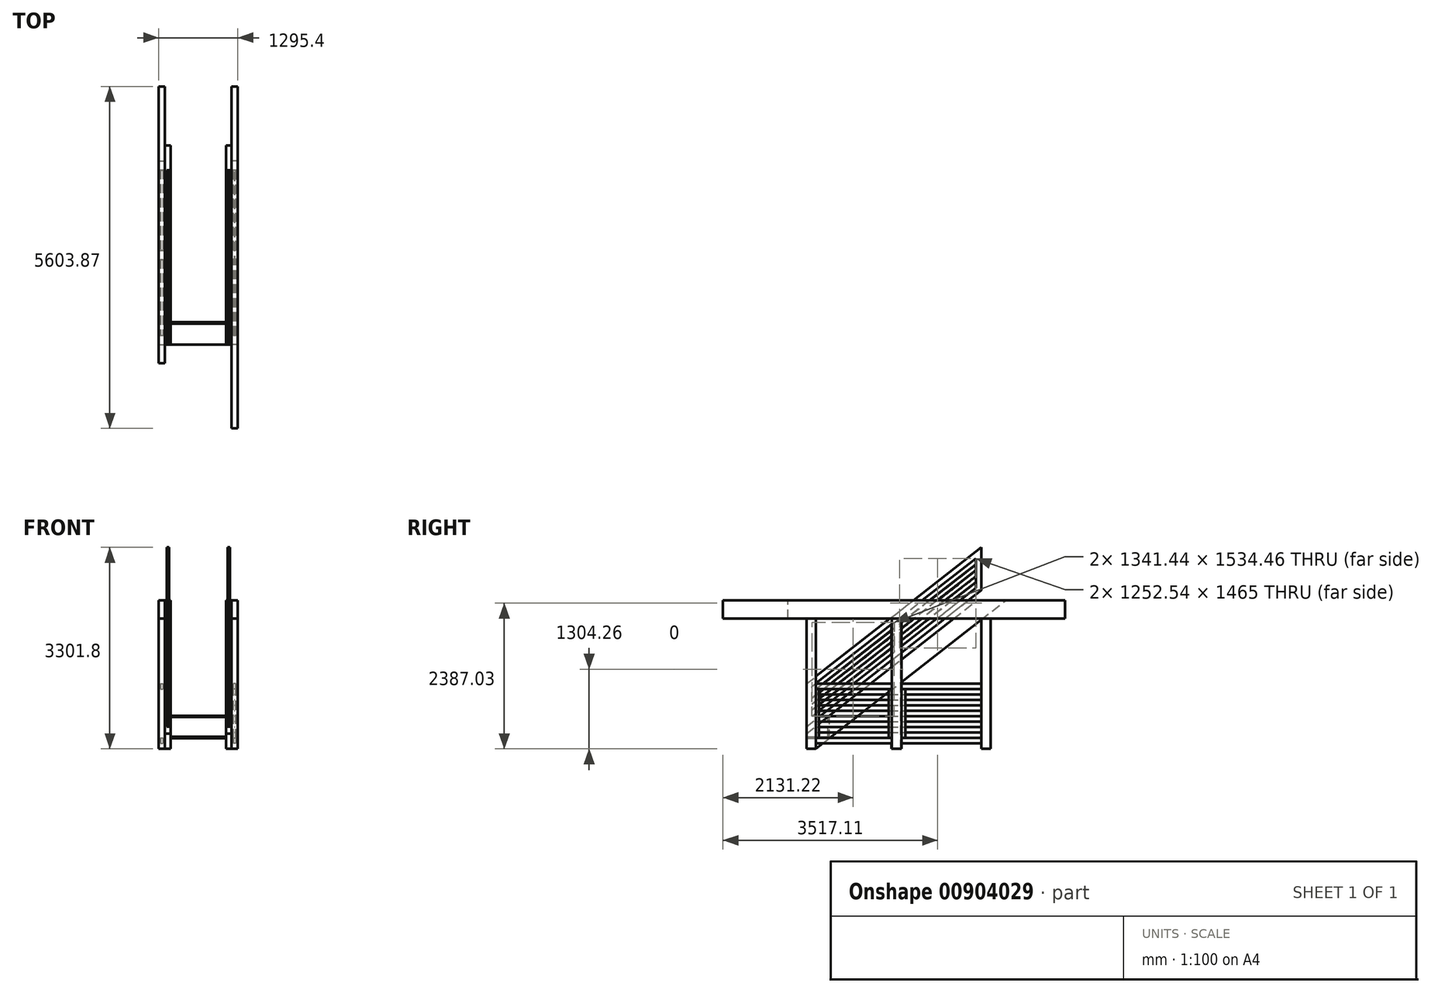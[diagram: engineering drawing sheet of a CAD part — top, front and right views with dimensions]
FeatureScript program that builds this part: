
annotation { "Feature Type Name" : "Feature", "Feature Type Description" : "" }
export const myFeature = defineFeature(function(context is Context, id is Id, definition is map)
    precondition{}
    {
        {
            var Q0;
            Q0=qCreatedBy(makeId("Front.planeOp"),FACE);
            var sketch = newSketch(context, id + "F0", { "sketchPlane" : qUnion([Q0])});
            skLineSegment(sketch, "E0", {"start": v(-546.1, 0) * mm, "end": v(546.1, 0) * mm});
            skSolve(sketch);
        }
        {
            var Q0;
            Q0=sQuery(id+"F0.wireOp",VERTEX,"E0.end");
            var Q1;
            Q1=qCreatedBy(makeId("Right.planeOp"),FACE);
            cPlane(context, id + "F1", {"entities" : qUnion([Q0, Q1]), "cplaneType" : CPlaneType.PLANE_POINT, "offset" : 25.4 * mm, "width" : 152.4 * mm, "height" : 152.4 * mm});
        }
        {
            var Q0;
            Q0=qCreatedBy(id+"F1.planeOp",FACE);
            var sketch = newSketch(context, id + "F2", { "sketchPlane" : qUnion([Q0])});
            skLineSegment(sketch, "E1.bottom", {"start": v(0, 0) * mm, "end": v(152.4, 0) * mm});
            skLineSegment(sketch, "E1.top", {"start": v(0, 2133.6) * mm, "end": v(152.4, 2133.6) * mm});
            skLineSegment(sketch, "E1.left", {"start": v(0, 0) * mm, "end": v(0, 2133.6) * mm});
            skLineSegment(sketch, "E1.right", {"start": v(152.4, 0) * mm, "end": v(152.4, 2133.6) * mm});
            skLineSegment(sketch, "E2.bottom", {"start": v(1397, 0) * mm, "end": v(1552.58, 0) * mm});
            skLineSegment(sketch, "E2.top", {"start": v(1397, 2133.6) * mm, "end": v(1552.57, 2133.6) * mm});
            skLineSegment(sketch, "E2.left", {"start": v(1397, 0) * mm, "end": v(1397, 2133.6) * mm});
            skLineSegment(sketch, "E2.right", {"start": v(1552.58, 0) * mm, "end": v(1552.57, 2133.6) * mm});
            skLineSegment(sketch, "E3.bottom", {"start": v(2860.68, 0) * mm, "end": v(3013.08, 0) * mm});
            skLineSegment(sketch, "E3.top", {"start": v(2860.68, 2133.6) * mm, "end": v(3013.07, 2133.6) * mm});
            skLineSegment(sketch, "E3.left", {"start": v(2860.68, 0) * mm, "end": v(2860.68, 2133.6) * mm});
            skLineSegment(sketch, "E3.right", {"start": v(3013.08, 0) * mm, "end": v(3013.07, 2133.6) * mm});
            skLineSegment(sketch, "E4.bottom", {"start": v(-1371.6, 2432.05) * mm, "end": v(4232.28, 2432.05) * mm});
            skLineSegment(sketch, "E4.top", {"start": v(-1371.6, 2133.6) * mm, "end": v(4232.28, 2133.6) * mm, "construction": true});
            skLineSegment(sketch, "E4.left", {"start": v(-1371.6, 2432.05) * mm, "end": v(-1371.6, 2133.6) * mm});
            skLineSegment(sketch, "E4.right", {"start": v(4232.28, 2432.05) * mm, "end": v(4232.28, 2133.6) * mm});
            skSolve(sketch);
        }
        {
            var Q0;
            Q0=qSketchRegion(id+"F2",true);
            extrude(context, id + "F3", {"entities" : qUnion([Q0]), "depth" : 101.6 * mm, "offsetDistance" : 25.4 * mm});
        }
        {
            var Q0;
            Q0=sQuery(id+"F0.wireOp",VERTEX,"E0.start");
            var Q1;
            Q1=qCreatedBy(makeId("Right.planeOp"),FACE);
            cPlane(context, id + "F4", {"entities" : qUnion([Q0, Q1]), "cplaneType" : CPlaneType.PLANE_POINT, "offset" : 25.4 * mm, "width" : 152.4 * mm, "height" : 152.4 * mm});
        }
        {
            var Q0;
            Q0=qCreatedBy(id+"F4.planeOp",FACE);
            var sketch = newSketch(context, id + "F5", { "sketchPlane" : qUnion([Q0])});
            skLineSegment(sketch, "E5.bottom", {"start": v(1390.65, 0) * mm, "end": v(1543.05, 0) * mm});
            skLineSegment(sketch, "E5.top", {"start": v(1390.65, 2133.6) * mm, "end": v(1543.05, 2133.6) * mm});
            skLineSegment(sketch, "E5.left", {"start": v(1390.65, 0) * mm, "end": v(1390.65, 2133.6) * mm});
            skLineSegment(sketch, "E5.right", {"start": v(1543.05, 0) * mm, "end": v(1543.05, 2133.6) * mm});
            skLineSegment(sketch, "E6.bottom", {"start": v(2863.85, 0) * mm, "end": v(3009.9, 0) * mm});
            skLineSegment(sketch, "E6.top", {"start": v(2863.85, 2133.6) * mm, "end": v(3009.9, 2133.6) * mm});
            skLineSegment(sketch, "E6.left", {"start": v(2863.85, 0) * mm, "end": v(2863.85, 2133.6) * mm});
            skLineSegment(sketch, "E6.right", {"start": v(3009.9, 0) * mm, "end": v(3009.9, 2133.6) * mm});
            skLineSegment(sketch, "E7.0.0", {"start": v(152.4, 2133.6) * mm, "end": v(0, 2133.6) * mm});
            skLineSegment(sketch, "E7.0.1", {"start": v(0, 2133.6) * mm, "end": v(0, 0) * mm});
            skLineSegment(sketch, "E7.0.2", {"start": v(0, 0) * mm, "end": v(152.4, 0) * mm});
            skLineSegment(sketch, "E7.0.3", {"start": v(152.4, 0) * mm, "end": v(152.4, 2133.6) * mm});
            skSolve(sketch);
        }
        {
            var Q0;
            Q0=qSketchRegion(id+"F5",true);
            extrude(context, id + "F6", {"entities" : qUnion([Q0]), "oppositeDirection" : true, "depth" : 101.6 * mm, "offsetDistance" : 25.4 * mm});
        }
        {
            var Q0;
            Q0=qCreatedBy(id+"F1.planeOp",FACE);
            var sketch = newSketch(context, id + "F7", { "sketchPlane" : qUnion([Q0])});
            skLineSegment(sketch, "E8.0", {"start": v(-1371.6, 2133.6) * mm, "end": v(4232.28, 2133.6) * mm});
            skLineSegment(sketch, "E9.0", {"start": v(-1371.6, 2432.05) * mm, "end": v(-1371.6, 2133.6) * mm});
            skLineSegment(sketch, "E10.0", {"start": v(-1371.6, 2432.05) * mm, "end": v(4232.28, 2432.05) * mm});
            skLineSegment(sketch, "E11.0", {"start": v(4232.28, 2432.05) * mm, "end": v(4232.28, 2133.6) * mm});
            skSolve(sketch);
        }
        {
            var Q0;
            Q0=makeQuery(id+"F7.imprint","IMPRINT",FACE,{"disambiguationData":[TD([[makeQuery(id+"F7.imprint","IMPRINT",EDGE,{"derivedFrom":sQuery(id+"F7.wireOp",EDGE,"E8.0")}),1.0]])]});
            var Q1;
            Q1=makeQuery(id+"F3.opExtrude","CAP_FACE",FACE,{"disambiguationData":[OSD([sQuery(id+"F2.wireOp",EDGE,"E1.bottom"),sQuery(id+"F2.wireOp",EDGE,"E1.top"),sQuery(id+"F2.wireOp",EDGE,"E1.left"),sQuery(id+"F2.wireOp",EDGE,"E1.right")])],"isStart":false});
            extrude(context, id + "F8", {"entities" : qUnion([Q0]), "endBound" : BoundingType.UP_TO_SURFACE, "depth" : 25.4 * mm, "endBoundEntityFace" : qUnion([Q1]), "offsetDistance" : 25.4 * mm});
        }
        {
            var Q0;
            Q0=qCreatedBy(id+"F4.planeOp",FACE);
            var sketch = newSketch(context, id + "F9", { "sketchPlane" : qUnion([Q0])});
            skLineSegment(sketch, "E12.0.0", {"start": v(4232.28, 2432.05) * mm, "end": v(4232.28, 2133.6) * mm});
            skLineSegment(sketch, "E12.0.1", {"start": v(4232.28, 2133.6) * mm, "end": v(-304.8, 2133.6) * mm});
            skLineSegment(sketch, "E12.0.3", {"start": v(-304.8, 2432.05) * mm, "end": v(4232.28, 2432.05) * mm});
            skLineSegment(sketch, "E13", {"start": v(-304.8, 2432.05) * mm, "end": v(-304.8, 2133.6) * mm});
            skPoint(sketch, "E12.0.2.end.orphan", {"position": v(-1371.6, 2432.05) * mm});
            skPoint(sketch, "E14.orphan", {"position": v(-1371.6, 2133.6) * mm});
            skSolve(sketch);
        }
        {
            var Q0;
            Q0=qSketchRegion(id+"F9",true);
            var Q1;
            Q1=makeQuery(id+"F6.opExtrude","CAP_FACE",FACE,{"disambiguationData":[OSD([sQuery(id+"F5.wireOp",EDGE,"E7.0.0"),sQuery(id+"F5.wireOp",EDGE,"E7.0.1"),sQuery(id+"F5.wireOp",EDGE,"E7.0.2"),sQuery(id+"F5.wireOp",EDGE,"E7.0.3")])],"isStart":false});
            extrude(context, id + "F10", {"entities" : qUnion([Q0]), "endBound" : BoundingType.UP_TO_SURFACE, "oppositeDirection" : true, "depth" : 25.4 * mm, "endBoundEntityFace" : qUnion([Q1]), "offsetDistance" : 25.4 * mm});
        }
        {
            var Q0;
            Q0=qCreatedBy(id+"F1.planeOp",FACE);
            var sketch = newSketch(context, id + "F11", { "sketchPlane" : qUnion([Q0])});
            skLineSegment(sketch, "E15.0", {"start": v(0, 0) * mm, "end": v(0, 251.61) * mm});
            skLineSegment(sketch, "E16", {"start": v(0, 251.61) * mm, "end": v(2790.83, 2432.05) * mm});
            skLineSegment(sketch, "E17", {"start": v(152.4, 0) * mm, "end": v(3265.28, 2432.05) * mm});
            skPoint(sketch, "E18.orphan", {"position": v(0, 2133.6) * mm});
            skPoint(sketch, "E19.orphan", {"position": v(152.4, 2133.6) * mm});
            skLineSegment(sketch, "E20.0", {"start": v(0, 0) * mm, "end": v(152.4, 0) * mm});
            skLineSegment(sketch, "E21.0", {"start": v(2790.83, 2432.05) * mm, "end": v(3265.28, 2432.05) * mm});
            skPoint(sketch, "E22.orphan", {"position": v(4232.28, 2432.05) * mm});
            skPoint(sketch, "E23.orphan", {"position": v(-1371.6, 2432.05) * mm});
            skPoint(sketch, "E24.0.end.orphan", {"position": v(3013.07, 2133.6) * mm});
            skPoint(sketch, "E24.0.start.orphan", {"position": v(3013.08, 0) * mm});
            skSolve(sketch);
        }
        {
            var Q0;
            Q0=qSketchRegion(id+"F11",true);
            extrude(context, id + "F12", {"entities" : qUnion([Q0]), "oppositeDirection" : true, "depth" : 92.07 * mm, "offsetDistance" : 25.4 * mm});
        }
        {
            var Q0;
            Q0=makeQuery(id+"F12.opExtrude","SWEPT_BODY",BODY,{"disambiguationData":[OSD([sQuery(id+"F11.wireOp",EDGE,"E15.0"),sQuery(id+"F11.wireOp",EDGE,"E16"),sQuery(id+"F11.wireOp",EDGE,"E17"),sQuery(id+"F11.wireOp",EDGE,"E20.0"),sQuery(id+"F11.wireOp",EDGE,"E21.0")])]});
            var Q1;
            Q1=qCreatedBy(makeId("Right.planeOp"),FACE);
            mirror(context, id + "F13", {"entities" : qUnion([Q0]), "mirrorPlane" : qUnion([Q1])});
        }
        {
            var Q0;
            Q0=makeQuery(id+"F3.opExtrude","CAP_FACE",FACE,{"disambiguationData":[OSD([sQuery(id+"F2.wireOp",EDGE,"E1.bottom"),sQuery(id+"F2.wireOp",EDGE,"E1.top"),sQuery(id+"F2.wireOp",EDGE,"E1.left"),sQuery(id+"F2.wireOp",EDGE,"E1.right")])],"isStart":false});
            var Q1;
            Q1=makeQuery(id+"F2.imprint","IMPRINT",FACE,{"disambiguationData":[TD([[makeQuery(id+"F2.imprint","IMPRINT",EDGE,{"derivedFrom":sQuery(id+"F2.wireOp",EDGE,"E1.bottom")}),1.0]])]});
            cPlane(context, id + "F14", {"entities" : qUnion([Q0, Q1]), "cplaneType" : CPlaneType.MID_PLANE, "offset" : 25.4 * mm, "width" : 152.4 * mm, "height" : 152.4 * mm});
        }
        {
            var Q0;
            Q0=qCreatedBy(id+"F14.planeOp",FACE);
            var sketch = newSketch(context, id + "F15", { "sketchPlane" : qUnion([Q0])});
            skLineSegment(sketch, "E25.0", {"start": v(152.4, 977.9) * mm, "end": v(152.4, 1066.8) * mm});
            skLineSegment(sketch, "E26.0", {"start": v(1397, 977.9) * mm, "end": v(1397, 1066.8) * mm});
            skLineSegment(sketch, "E27.bottom", {"start": v(152.4, 1066.8) * mm, "end": v(1397, 1066.8) * mm});
            skLineSegment(sketch, "E27.top", {"start": v(152.4, 977.9) * mm, "end": v(1397, 977.9) * mm});
            skPoint(sketch, "E28.orphan", {"position": v(152.4, 2133.6) * mm});
            skPoint(sketch, "E29.orphan", {"position": v(1397, 2133.6) * mm});
            skPoint(sketch, "E30.orphan", {"position": v(1397, 0) * mm});
            skPoint(sketch, "E31.orphan", {"position": v(152.4, 0) * mm});
            skLineSegment(sketch, "E32.bottom", {"start": v(1552.58, 1066.8) * mm, "end": v(2860.68, 1066.8) * mm});
            skLineSegment(sketch, "E32.top", {"start": v(1552.58, 977.9) * mm, "end": v(2860.68, 977.9) * mm});
            skLineSegment(sketch, "E32.left", {"start": v(1552.58, 1066.8) * mm, "end": v(1552.58, 977.9) * mm});
            skLineSegment(sketch, "E32.right", {"start": v(2860.68, 1066.8) * mm, "end": v(2860.68, 977.9) * mm});
            skLineSegment(sketch, "E33.bottom", {"start": v(152.4, 177.8) * mm, "end": v(1397, 177.8) * mm});
            skLineSegment(sketch, "E33.top", {"start": v(152.4, 88.9) * mm, "end": v(1397, 88.9) * mm});
            skLineSegment(sketch, "E33.left", {"start": v(152.4, 177.8) * mm, "end": v(152.4, 88.9) * mm});
            skLineSegment(sketch, "E33.right", {"start": v(1397, 177.8) * mm, "end": v(1397, 88.9) * mm});
            skLineSegment(sketch, "E34.bottom", {"start": v(1552.58, 177.8) * mm, "end": v(2860.68, 177.8) * mm});
            skLineSegment(sketch, "E34.top", {"start": v(1552.58, 88.9) * mm, "end": v(2860.68, 88.9) * mm});
            skLineSegment(sketch, "E34.left", {"start": v(1552.58, 177.8) * mm, "end": v(1552.58, 88.9) * mm});
            skLineSegment(sketch, "E34.right", {"start": v(2860.68, 177.8) * mm, "end": v(2860.68, 88.9) * mm});
            skSolve(sketch);
        }
        {
            var Q0;
            Q0=qSketchRegion(id+"F15",true);
            extrude(context, id + "F16", {"entities" : qUnion([Q0]), "endBound" : BoundingType.SYMMETRIC, "depth" : 38.1 * mm, "offsetDistance" : 25.4 * mm});
        }
        {
            var Q0;
            Q0=makeQuery(id+"F16.opExtrude","CAP_EDGE",EDGE,{"disambiguationData":[OSD([sQuery(id+"F15.wireOp",EDGE,"E27.top")])],"isStart":false});
            cPoint(context, id + "F17", {"entities" : qUnion([Q0]), "parameter" : 0.5});
        }
        {
            var Q0;
            Q0=qCreatedBy(id+"F17",VERTEX);
            var Q1;
            Q1=qCreatedBy(makeId("Front.planeOp"),FACE);
            cPlane(context, id + "F18", {"entities" : qUnion([Q0, Q1]), "cplaneType" : CPlaneType.PLANE_POINT, "offset" : 25.4 * mm, "width" : 152.4 * mm, "height" : 152.4 * mm});
        }
        {
            var Q0;
            Q0=qCreatedBy(id+"F18.planeOp",FACE);
            var sketch = newSketch(context, id + "F19", { "sketchPlane" : qUnion([Q0])});
            skLineSegment(sketch, "E35", {"start": v(596.9, 977.9) * mm, "end": v(596.9, 889) * mm, "construction": true});
            skLineSegment(sketch, "E36", {"start": v(596.9, 889) * mm, "end": v(596.9, 800.1) * mm, "construction": true});
            skLineSegment(sketch, "E37", {"start": v(596.9, 800.1) * mm, "end": v(596.9, 711.2) * mm, "construction": true});
            skLineSegment(sketch, "E38", {"start": v(596.9, 711.2) * mm, "end": v(596.9, 622.3) * mm, "construction": true});
            skLineSegment(sketch, "E39", {"start": v(596.9, 622.3) * mm, "end": v(596.9, 533.4) * mm, "construction": true});
            skLineSegment(sketch, "E40", {"start": v(596.9, 533.4) * mm, "end": v(596.9, 444.5) * mm, "construction": true});
            skLineSegment(sketch, "E41", {"start": v(596.9, 444.5) * mm, "end": v(596.9, 355.6) * mm, "construction": true});
            skLineSegment(sketch, "E42", {"start": v(596.9, 355.6) * mm, "end": v(596.9, 266.7) * mm, "construction": true});
            skLineSegment(sketch, "E43", {"start": v(596.9, 266.7) * mm, "end": v(596.9, 177.8) * mm, "construction": true});
            skCircle(sketch, "E44", {"center": v(596.9, 889) * mm, "radius": 1.59 * mm});
            skCircle(sketch, "E45", {"center": v(596.9, 800.1) * mm, "radius": 1.59 * mm});
            skCircle(sketch, "E46", {"center": v(596.9, 711.2) * mm, "radius": 1.59 * mm});
            skCircle(sketch, "E47", {"center": v(596.9, 622.3) * mm, "radius": 1.59 * mm});
            skCircle(sketch, "E48", {"center": v(596.9, 533.4) * mm, "radius": 1.59 * mm});
            skCircle(sketch, "E49", {"center": v(596.9, 444.5) * mm, "radius": 1.59 * mm});
            skCircle(sketch, "E50", {"center": v(596.9, 355.6) * mm, "radius": 1.59 * mm});
            skCircle(sketch, "E51", {"center": v(596.9, 266.7) * mm, "radius": 1.59 * mm});
            skSolve(sketch);
        }
        {
            var Q0;
            Q0 = qSketchRegion(id + "F19", true);
            var Q1;
            Q1=makeQuery(id+"F3.opExtrude","SWEPT_FACE",FACE,{"disambiguationData":[OSD([sQuery(id+"F2.wireOp",EDGE,"E3.left")])]});
            extrude(context, id + "F20", {"entities" : qUnion([Q0]), "endBound" : BoundingType.UP_TO_NEXT, "depth" : 25.4 * mm, "offsetDistance" : 25.4 * mm, "hasSecondDirection" : true, "secondDirectionBound" : SecondDirectionBoundingType.UP_TO_SURFACE, "secondDirectionOppositeDirection" : true, "secondDirectionDepth" : 25.4 * mm, "secondDirectionBoundEntityFace" : qUnion([Q1])});
        }
        {
            var Q0;
            Q0=makeQuery(id+"F6.opExtrude","CAP_FACE",FACE,{"disambiguationData":[OSD([sQuery(id+"F5.wireOp",EDGE,"E7.0.0"),sQuery(id+"F5.wireOp",EDGE,"E7.0.1"),sQuery(id+"F5.wireOp",EDGE,"E7.0.2"),sQuery(id+"F5.wireOp",EDGE,"E7.0.3")])],"isStart":false});
            var Q1;
            Q1=makeQuery(id+"F6.opExtrude","CAP_FACE",FACE,{"disambiguationData":[OSD([sQuery(id+"F5.wireOp",EDGE,"E7.0.0"),sQuery(id+"F5.wireOp",EDGE,"E7.0.1"),sQuery(id+"F5.wireOp",EDGE,"E7.0.2"),sQuery(id+"F5.wireOp",EDGE,"E7.0.3")])],"isStart":true});
            cPlane(context, id + "F21", {"entities" : qUnion([Q0, Q1]), "cplaneType" : CPlaneType.MID_PLANE, "offset" : 25.4 * mm, "width" : 152.4 * mm, "height" : 152.4 * mm});
        }
        {
            var Q0;
            Q0=qCreatedBy(id+"F21.planeOp",FACE);
            var sketch = newSketch(context, id + "F22", { "sketchPlane" : qUnion([Q0])});
            skLineSegment(sketch, "E52.bottom", {"start": v(-1397, 1066.8) * mm, "end": v(-152.4, 1066.8) * mm});
            skLineSegment(sketch, "E52.top", {"start": v(-1397, 977.9) * mm, "end": v(-152.4, 977.9) * mm});
            skLineSegment(sketch, "E52.left", {"start": v(-1397, 1066.8) * mm, "end": v(-1397, 977.9) * mm});
            skLineSegment(sketch, "E52.right", {"start": v(-152.4, 1066.8) * mm, "end": v(-152.4, 977.9) * mm});
            skLineSegment(sketch, "E53.bottom", {"start": v(-1397, 177.8) * mm, "end": v(-152.4, 177.8) * mm});
            skLineSegment(sketch, "E53.top", {"start": v(-1397, 88.9) * mm, "end": v(-152.4, 88.9) * mm});
            skLineSegment(sketch, "E53.left", {"start": v(-1397, 177.8) * mm, "end": v(-1397, 88.9) * mm});
            skLineSegment(sketch, "E53.right", {"start": v(-152.4, 177.8) * mm, "end": v(-152.4, 88.9) * mm});
            skLineSegment(sketch, "E54.bottom", {"start": v(-2860.68, 1066.8) * mm, "end": v(-1552.58, 1066.8) * mm});
            skLineSegment(sketch, "E54.top", {"start": v(-2860.68, 977.9) * mm, "end": v(-1552.58, 977.9) * mm});
            skLineSegment(sketch, "E54.left", {"start": v(-2860.68, 1066.8) * mm, "end": v(-2860.68, 977.9) * mm});
            skLineSegment(sketch, "E54.right", {"start": v(-1552.58, 1066.8) * mm, "end": v(-1552.58, 977.9) * mm});
            skLineSegment(sketch, "E55.bottom", {"start": v(-2860.68, 177.8) * mm, "end": v(-1552.58, 177.8) * mm});
            skLineSegment(sketch, "E55.top", {"start": v(-2860.68, 88.9) * mm, "end": v(-1552.58, 88.9) * mm});
            skLineSegment(sketch, "E55.left", {"start": v(-2860.68, 177.8) * mm, "end": v(-2860.68, 88.9) * mm});
            skLineSegment(sketch, "E55.right", {"start": v(-1552.58, 177.8) * mm, "end": v(-1552.58, 88.9) * mm});
            skSolve(sketch);
        }
        {
            var Q0;
            Q0=qSketchRegion(id+"F22",true);
            extrude(context, id + "F23", {"entities" : qUnion([Q0]), "endBound" : BoundingType.SYMMETRIC, "depth" : 38.1 * mm, "offsetDistance" : 25.4 * mm});
        }
        {
            var Q0;
            Q0=makeQuery(id+"F12.opExtrude","CAP_FACE",FACE,{"disambiguationData":[OSD([sQuery(id+"F11.wireOp",EDGE,"E15.0"),sQuery(id+"F11.wireOp",EDGE,"E16"),sQuery(id+"F11.wireOp",EDGE,"E17"),sQuery(id+"F11.wireOp",EDGE,"E20.0"),sQuery(id+"F11.wireOp",EDGE,"E21.0")])],"isStart":false});
            var Q1;
            Q1=makeQuery(id+"F12.opExtrude","CAP_FACE",FACE,{"disambiguationData":[OSD([sQuery(id+"F11.wireOp",EDGE,"E15.0"),sQuery(id+"F11.wireOp",EDGE,"E16"),sQuery(id+"F11.wireOp",EDGE,"E17"),sQuery(id+"F11.wireOp",EDGE,"E20.0"),sQuery(id+"F11.wireOp",EDGE,"E21.0")])],"isStart":true});
            cPlane(context, id + "F24", {"entities" : qUnion([Q0, Q1]), "cplaneType" : CPlaneType.MID_PLANE, "offset" : 25.4 * mm, "width" : 152.4 * mm, "height" : 152.4 * mm});
        }
        {
            var Q0;
            Q0=qCreatedBy(id+"F24.planeOp",FACE);
            var sketch = newSketch(context, id + "F25", { "sketchPlane" : qUnion([Q0])});
            skLineSegment(sketch, "E56.0", {"start": v(0, 364.43) * mm, "end": v(-2860.68, 2599.43) * mm});
            skLineSegment(sketch, "E57.0", {"start": v(0, 1066.8) * mm, "end": v(-2860.68, 3301.8) * mm});
            skLineSegment(sketch, "E58.0", {"start": v(0, 364.43) * mm, "end": v(0, 1066.8) * mm});
            skPoint(sketch, "E59.orphan", {"position": v(0, 2133.6) * mm});
            skPoint(sketch, "E60.orphan", {"position": v(0, 0) * mm});
            skLineSegment(sketch, "E61", {"start": v(-2860.68, 3301.8) * mm, "end": v(-2860.68, 2599.43) * mm});
            skLineSegment(sketch, "E62.0", {"start": v(-88.9, 1023.44) * mm, "end": v(-2771.78, 3119.53) * mm});
            skLineSegment(sketch, "E63.0", {"start": v(-88.9, 537.03) * mm, "end": v(-88.9, 1023.44) * mm});
            skLineSegment(sketch, "E64.trimOffspring", {"start": v(-2771.78, 3119.53) * mm, "end": v(-2771.78, 2633.12) * mm});
            skLineSegment(sketch, "E65.trimOffspring", {"start": v(-88.9, 537.03) * mm, "end": v(-2771.78, 2633.12) * mm});
            skLineSegment(sketch, "E66", {"start": v(-88.9, 1023.44) * mm, "end": v(0, 1066.8) * mm});
            skLineSegment(sketch, "E67", {"start": v(0, 364.43) * mm, "end": v(-88.9, 537.03) * mm});
            skLineSegment(sketch, "E68", {"start": v(-2771.78, 3119.53) * mm, "end": v(-2860.68, 3301.8) * mm});
            skLineSegment(sketch, "E69", {"start": v(-2771.78, 2633.12) * mm, "end": v(-2860.68, 2599.43) * mm});
            skPoint(sketch, "E70.0.start.orphan", {"position": v(-1552.58, 0) * mm});
            skPoint(sketch, "E71.0.start.orphan", {"position": v(-1397, 0) * mm});
            skLineSegment(sketch, "E72", {"start": v(-1397, 2045.44) * mm, "end": v(-1552.57, 2045.44) * mm, "construction": true});
            skLineSegment(sketch, "E73", {"start": v(-1474.79, 2045.44) * mm, "end": v(-1474.79, 1619.8) * mm, "construction": true});
            skLineSegment(sketch, "E74", {"start": v(-1430.34, 2071.49) * mm, "end": v(-1430.34, 1585.08) * mm});
            skLineSegment(sketch, "E75.MirrorCS", {"start": v(-1519.24, 2140.94) * mm, "end": v(-1519.24, 1654.53) * mm});
            skLineSegment(sketch, "E76", {"start": v(-1474.79, 1619.8) * mm, "end": v(-1238.8, 1921.85) * mm, "construction": true});
            skSolve(sketch);
        }
        {
            var Q0;
            Q0=makeQuery(id+"F25.imprint","IMPRINT",FACE,{"disambiguationData":[TD([[makeQuery(id+"F25.imprint","IMPRINT",EDGE,{"derivedFrom":sQuery(id+"F25.wireOp",EDGE,"E57.0")}),1.0]])]});
            var Q1;
            Q1=makeQuery(id+"F25.imprint","IMPRINT",FACE,{"disambiguationData":[TD([[makeQuery(id+"F25.imprint","IMPRINT",EDGE,{"derivedFrom":sQuery(id+"F25.wireOp",EDGE,"E61")}),1.0]])]});
            var Q2;
            Q2=makeQuery(id+"F25.imprint","IMPRINT",FACE,{"disambiguationData":[TD([[makeQuery(id+"F25.imprint","IMPRINT",EDGE,{"derivedFrom":sQuery(id+"F25.wireOp",EDGE,"E56.0")}),-1.0]])]});
            var Q3;
            Q3=makeQuery(id+"F25.imprint","IMPRINT",FACE,{"disambiguationData":[TD([[makeQuery(id+"F25.imprint","IMPRINT",EDGE,{"derivedFrom":sQuery(id+"F25.wireOp",EDGE,"E58.0")}),1.0]])]});
            var Q4;
            {var subQ0=sQuery(id+"F25.wireOp",EDGE,"E74");Q4=makeQuery(id+"F25.imprint","IMPRINT",FACE,{"disambiguationData":[TD([[makeQuery(id+"F25.imprint","IMPRINT",EDGE,{"derivedFrom":subQ0}),-1.0]])]});}
            extrude(context, id + "F26", {"entities" : qUnion([Q0, Q1, Q2, Q3, Q4]), "endBound" : BoundingType.SYMMETRIC, "depth" : 38.1 * mm, "offsetDistance" : 25.4 * mm});
        }
        {
            var Q0;
            Q0=makeQuery(id+"FHlwvRDlp0Xm9cG_28.opPattern","COPY",BODY,{"derivedFrom":makeQuery(id+"F8SUDAKNwE7EsUo_26.opExtrude","SWEPT_BODY",BODY,{"disambiguationData":[OSD([sQuery(id+"FL15oFyUtI3aBrd_26.wireOp",EDGE,"VrMjjD4X-CYQ3-yA4v-7hPQ-fvzbZlASwizG"),sQuery(id+"FL15oFyUtI3aBrd_26.wireOp",EDGE,"w2hLujtV-I2TP-pglX-lp1i-IlIAiG8QoFdS"),sQuery(id+"FL15oFyUtI3aBrd_26.wireOp",EDGE,"Haosjz9O-undc-fuWQ-oRTa-weX78iZNw2A3"),sQuery(id+"FL15oFyUtI3aBrd_26.wireOp",EDGE,"bgq73AYN-j48V-VU7J-jVlr-Mn434VgHHMK9")])]}),"instanceName":"6"});
            var Q1;
            Q1=makeQuery(id+"FHlwvRDlp0Xm9cG_28.opPattern","COPY",BODY,{"derivedFrom":makeQuery(id+"F8SUDAKNwE7EsUo_26.opExtrude","SWEPT_BODY",BODY,{"disambiguationData":[OSD([sQuery(id+"FL15oFyUtI3aBrd_26.wireOp",EDGE,"VrMjjD4X-CYQ3-yA4v-7hPQ-fvzbZlASwizG"),sQuery(id+"FL15oFyUtI3aBrd_26.wireOp",EDGE,"w2hLujtV-I2TP-pglX-lp1i-IlIAiG8QoFdS"),sQuery(id+"FL15oFyUtI3aBrd_26.wireOp",EDGE,"Haosjz9O-undc-fuWQ-oRTa-weX78iZNw2A3"),sQuery(id+"FL15oFyUtI3aBrd_26.wireOp",EDGE,"bgq73AYN-j48V-VU7J-jVlr-Mn434VgHHMK9")])]}),"instanceName":"5"});
            var Q2;
            Q2=makeQuery(id+"FHlwvRDlp0Xm9cG_28.opPattern","COPY",BODY,{"derivedFrom":makeQuery(id+"F8SUDAKNwE7EsUo_26.opExtrude","SWEPT_BODY",BODY,{"disambiguationData":[OSD([sQuery(id+"FL15oFyUtI3aBrd_26.wireOp",EDGE,"VrMjjD4X-CYQ3-yA4v-7hPQ-fvzbZlASwizG"),sQuery(id+"FL15oFyUtI3aBrd_26.wireOp",EDGE,"w2hLujtV-I2TP-pglX-lp1i-IlIAiG8QoFdS"),sQuery(id+"FL15oFyUtI3aBrd_26.wireOp",EDGE,"Haosjz9O-undc-fuWQ-oRTa-weX78iZNw2A3"),sQuery(id+"FL15oFyUtI3aBrd_26.wireOp",EDGE,"bgq73AYN-j48V-VU7J-jVlr-Mn434VgHHMK9")])]}),"instanceName":"4"});
            var Q3;
            Q3=makeQuery(id+"F2WfsVXshQW02Ji_28.opPattern","COPY",BODY,{"derivedFrom":makeQuery(id+"F8SUDAKNwE7EsUo_26.opExtrude","SWEPT_BODY",BODY,{"disambiguationData":[OSD([sQuery(id+"FL15oFyUtI3aBrd_26.wireOp",EDGE,"VrMjjD4X-CYQ3-yA4v-7hPQ-fvzbZlASwizG"),sQuery(id+"FL15oFyUtI3aBrd_26.wireOp",EDGE,"w2hLujtV-I2TP-pglX-lp1i-IlIAiG8QoFdS"),sQuery(id+"FL15oFyUtI3aBrd_26.wireOp",EDGE,"Haosjz9O-undc-fuWQ-oRTa-weX78iZNw2A3"),sQuery(id+"FL15oFyUtI3aBrd_26.wireOp",EDGE,"bgq73AYN-j48V-VU7J-jVlr-Mn434VgHHMK9")])]}),"instanceName":"1"});
            var Q4;
            Q4=makeQuery(id+"F2WfsVXshQW02Ji_28.opPattern","COPY",BODY,{"derivedFrom":makeQuery(id+"F8SUDAKNwE7EsUo_26.opExtrude","SWEPT_BODY",BODY,{"disambiguationData":[OSD([sQuery(id+"FL15oFyUtI3aBrd_26.wireOp",EDGE,"VrMjjD4X-CYQ3-yA4v-7hPQ-fvzbZlASwizG"),sQuery(id+"FL15oFyUtI3aBrd_26.wireOp",EDGE,"w2hLujtV-I2TP-pglX-lp1i-IlIAiG8QoFdS"),sQuery(id+"FL15oFyUtI3aBrd_26.wireOp",EDGE,"Haosjz9O-undc-fuWQ-oRTa-weX78iZNw2A3"),sQuery(id+"FL15oFyUtI3aBrd_26.wireOp",EDGE,"bgq73AYN-j48V-VU7J-jVlr-Mn434VgHHMK9")])]}),"instanceName":"2"});
            var Q5;
            Q5=makeQuery(id+"F2WfsVXshQW02Ji_28.opPattern","COPY",BODY,{"derivedFrom":makeQuery(id+"F8SUDAKNwE7EsUo_26.opExtrude","SWEPT_BODY",BODY,{"disambiguationData":[OSD([sQuery(id+"FL15oFyUtI3aBrd_26.wireOp",EDGE,"VrMjjD4X-CYQ3-yA4v-7hPQ-fvzbZlASwizG"),sQuery(id+"FL15oFyUtI3aBrd_26.wireOp",EDGE,"w2hLujtV-I2TP-pglX-lp1i-IlIAiG8QoFdS"),sQuery(id+"FL15oFyUtI3aBrd_26.wireOp",EDGE,"Haosjz9O-undc-fuWQ-oRTa-weX78iZNw2A3"),sQuery(id+"FL15oFyUtI3aBrd_26.wireOp",EDGE,"bgq73AYN-j48V-VU7J-jVlr-Mn434VgHHMK9")])]}),"instanceName":"3"});
            var Q6;
            Q6=makeQuery(id+"F2WfsVXshQW02Ji_28.opPattern","COPY",BODY,{"derivedFrom":makeQuery(id+"F8SUDAKNwE7EsUo_26.opExtrude","SWEPT_BODY",BODY,{"disambiguationData":[OSD([sQuery(id+"FL15oFyUtI3aBrd_26.wireOp",EDGE,"VrMjjD4X-CYQ3-yA4v-7hPQ-fvzbZlASwizG"),sQuery(id+"FL15oFyUtI3aBrd_26.wireOp",EDGE,"w2hLujtV-I2TP-pglX-lp1i-IlIAiG8QoFdS"),sQuery(id+"FL15oFyUtI3aBrd_26.wireOp",EDGE,"Haosjz9O-undc-fuWQ-oRTa-weX78iZNw2A3"),sQuery(id+"FL15oFyUtI3aBrd_26.wireOp",EDGE,"bgq73AYN-j48V-VU7J-jVlr-Mn434VgHHMK9")])]}),"instanceName":"4"});
            var Q7;
            Q7=makeQuery(id+"F2WfsVXshQW02Ji_28.opPattern","COPY",BODY,{"derivedFrom":makeQuery(id+"F8SUDAKNwE7EsUo_26.opExtrude","SWEPT_BODY",BODY,{"disambiguationData":[OSD([sQuery(id+"FL15oFyUtI3aBrd_26.wireOp",EDGE,"VrMjjD4X-CYQ3-yA4v-7hPQ-fvzbZlASwizG"),sQuery(id+"FL15oFyUtI3aBrd_26.wireOp",EDGE,"w2hLujtV-I2TP-pglX-lp1i-IlIAiG8QoFdS"),sQuery(id+"FL15oFyUtI3aBrd_26.wireOp",EDGE,"Haosjz9O-undc-fuWQ-oRTa-weX78iZNw2A3"),sQuery(id+"FL15oFyUtI3aBrd_26.wireOp",EDGE,"bgq73AYN-j48V-VU7J-jVlr-Mn434VgHHMK9")])]}),"instanceName":"5"});
            var Q8;
            Q8=makeQuery(id+"F2WfsVXshQW02Ji_28.opPattern","COPY",BODY,{"derivedFrom":makeQuery(id+"F8SUDAKNwE7EsUo_26.opExtrude","SWEPT_BODY",BODY,{"disambiguationData":[OSD([sQuery(id+"FL15oFyUtI3aBrd_26.wireOp",EDGE,"VrMjjD4X-CYQ3-yA4v-7hPQ-fvzbZlASwizG"),sQuery(id+"FL15oFyUtI3aBrd_26.wireOp",EDGE,"w2hLujtV-I2TP-pglX-lp1i-IlIAiG8QoFdS"),sQuery(id+"FL15oFyUtI3aBrd_26.wireOp",EDGE,"Haosjz9O-undc-fuWQ-oRTa-weX78iZNw2A3"),sQuery(id+"FL15oFyUtI3aBrd_26.wireOp",EDGE,"bgq73AYN-j48V-VU7J-jVlr-Mn434VgHHMK9")])]}),"instanceName":"6"});
            var Q9;
            Q9=makeQuery(id+"FHlwvRDlp0Xm9cG_28.opPattern","COPY",BODY,{"derivedFrom":makeQuery(id+"F8SUDAKNwE7EsUo_26.opExtrude","SWEPT_BODY",BODY,{"disambiguationData":[OSD([sQuery(id+"FL15oFyUtI3aBrd_26.wireOp",EDGE,"VrMjjD4X-CYQ3-yA4v-7hPQ-fvzbZlASwizG"),sQuery(id+"FL15oFyUtI3aBrd_26.wireOp",EDGE,"w2hLujtV-I2TP-pglX-lp1i-IlIAiG8QoFdS"),sQuery(id+"FL15oFyUtI3aBrd_26.wireOp",EDGE,"Haosjz9O-undc-fuWQ-oRTa-weX78iZNw2A3"),sQuery(id+"FL15oFyUtI3aBrd_26.wireOp",EDGE,"bgq73AYN-j48V-VU7J-jVlr-Mn434VgHHMK9")])]}),"instanceName":"1"});
            var Q10;
            Q10=makeQuery(id+"FHlwvRDlp0Xm9cG_28.opPattern","COPY",BODY,{"derivedFrom":makeQuery(id+"F8SUDAKNwE7EsUo_26.opExtrude","SWEPT_BODY",BODY,{"disambiguationData":[OSD([sQuery(id+"FL15oFyUtI3aBrd_26.wireOp",EDGE,"VrMjjD4X-CYQ3-yA4v-7hPQ-fvzbZlASwizG"),sQuery(id+"FL15oFyUtI3aBrd_26.wireOp",EDGE,"w2hLujtV-I2TP-pglX-lp1i-IlIAiG8QoFdS"),sQuery(id+"FL15oFyUtI3aBrd_26.wireOp",EDGE,"Haosjz9O-undc-fuWQ-oRTa-weX78iZNw2A3"),sQuery(id+"FL15oFyUtI3aBrd_26.wireOp",EDGE,"bgq73AYN-j48V-VU7J-jVlr-Mn434VgHHMK9")])]}),"instanceName":"2"});
            var Q11;
            Q11=makeQuery(id+"FHlwvRDlp0Xm9cG_28.opPattern","COPY",BODY,{"derivedFrom":makeQuery(id+"F8SUDAKNwE7EsUo_26.opExtrude","SWEPT_BODY",BODY,{"disambiguationData":[OSD([sQuery(id+"FL15oFyUtI3aBrd_26.wireOp",EDGE,"VrMjjD4X-CYQ3-yA4v-7hPQ-fvzbZlASwizG"),sQuery(id+"FL15oFyUtI3aBrd_26.wireOp",EDGE,"w2hLujtV-I2TP-pglX-lp1i-IlIAiG8QoFdS"),sQuery(id+"FL15oFyUtI3aBrd_26.wireOp",EDGE,"Haosjz9O-undc-fuWQ-oRTa-weX78iZNw2A3"),sQuery(id+"FL15oFyUtI3aBrd_26.wireOp",EDGE,"bgq73AYN-j48V-VU7J-jVlr-Mn434VgHHMK9")])]}),"instanceName":"3"});
            var Q12;
            Q12=makeQuery(id+"FeZcZVifgtCtkFP_28.opPattern","COPY",BODY,{"derivedFrom":makeQuery(id+"F8SUDAKNwE7EsUo_26.opExtrude","SWEPT_BODY",BODY,{"disambiguationData":[OSD([sQuery(id+"FL15oFyUtI3aBrd_26.wireOp",EDGE,"r1ENYqX6-6cbb-IXZZ-OYHh-hil2T0saHPIk"),sQuery(id+"FL15oFyUtI3aBrd_26.wireOp",EDGE,"urqhdUsR-mYzn-lPOw-VYYU-hiYjFugUIPjQ"),sQuery(id+"FL15oFyUtI3aBrd_26.wireOp",EDGE,"n4ZBWz9C-kEvr-YDfq-9QLi-Q9yPjt8Ly8hL"),sQuery(id+"FL15oFyUtI3aBrd_26.wireOp",EDGE,"e2zvSQfy-2Bil-96lf-zHMV-ZBLVYw9i9ZqR")])]}),"instanceName":"4"});
            var Q13;
            Q13=makeQuery(id+"FeZcZVifgtCtkFP_28.opPattern","COPY",BODY,{"derivedFrom":makeQuery(id+"F8SUDAKNwE7EsUo_26.opExtrude","SWEPT_BODY",BODY,{"disambiguationData":[OSD([sQuery(id+"FL15oFyUtI3aBrd_26.wireOp",EDGE,"r1ENYqX6-6cbb-IXZZ-OYHh-hil2T0saHPIk"),sQuery(id+"FL15oFyUtI3aBrd_26.wireOp",EDGE,"urqhdUsR-mYzn-lPOw-VYYU-hiYjFugUIPjQ"),sQuery(id+"FL15oFyUtI3aBrd_26.wireOp",EDGE,"n4ZBWz9C-kEvr-YDfq-9QLi-Q9yPjt8Ly8hL"),sQuery(id+"FL15oFyUtI3aBrd_26.wireOp",EDGE,"e2zvSQfy-2Bil-96lf-zHMV-ZBLVYw9i9ZqR")])]}),"instanceName":"5"});
            var Q14;
            Q14=makeQuery(id+"FeZcZVifgtCtkFP_28.opPattern","COPY",BODY,{"derivedFrom":makeQuery(id+"F8SUDAKNwE7EsUo_26.opExtrude","SWEPT_BODY",BODY,{"disambiguationData":[OSD([sQuery(id+"FL15oFyUtI3aBrd_26.wireOp",EDGE,"r1ENYqX6-6cbb-IXZZ-OYHh-hil2T0saHPIk"),sQuery(id+"FL15oFyUtI3aBrd_26.wireOp",EDGE,"urqhdUsR-mYzn-lPOw-VYYU-hiYjFugUIPjQ"),sQuery(id+"FL15oFyUtI3aBrd_26.wireOp",EDGE,"n4ZBWz9C-kEvr-YDfq-9QLi-Q9yPjt8Ly8hL"),sQuery(id+"FL15oFyUtI3aBrd_26.wireOp",EDGE,"e2zvSQfy-2Bil-96lf-zHMV-ZBLVYw9i9ZqR")])]}),"instanceName":"6"});
            var Q15;
            Q15=makeQuery(id+"FeZcZVifgtCtkFP_28.opPattern","COPY",BODY,{"derivedFrom":makeQuery(id+"F8SUDAKNwE7EsUo_26.opExtrude","SWEPT_BODY",BODY,{"disambiguationData":[OSD([sQuery(id+"FL15oFyUtI3aBrd_26.wireOp",EDGE,"r1ENYqX6-6cbb-IXZZ-OYHh-hil2T0saHPIk"),sQuery(id+"FL15oFyUtI3aBrd_26.wireOp",EDGE,"urqhdUsR-mYzn-lPOw-VYYU-hiYjFugUIPjQ"),sQuery(id+"FL15oFyUtI3aBrd_26.wireOp",EDGE,"n4ZBWz9C-kEvr-YDfq-9QLi-Q9yPjt8Ly8hL"),sQuery(id+"FL15oFyUtI3aBrd_26.wireOp",EDGE,"e2zvSQfy-2Bil-96lf-zHMV-ZBLVYw9i9ZqR")])]}),"instanceName":"7"});
            var Q16;
            Q16=makeQuery(id+"FVkHQME55aZ6rBw_28.opPattern","COPY",BODY,{"derivedFrom":makeQuery(id+"F8SUDAKNwE7EsUo_26.opExtrude","SWEPT_BODY",BODY,{"disambiguationData":[OSD([sQuery(id+"FL15oFyUtI3aBrd_26.wireOp",EDGE,"r1ENYqX6-6cbb-IXZZ-OYHh-hil2T0saHPIk"),sQuery(id+"FL15oFyUtI3aBrd_26.wireOp",EDGE,"urqhdUsR-mYzn-lPOw-VYYU-hiYjFugUIPjQ"),sQuery(id+"FL15oFyUtI3aBrd_26.wireOp",EDGE,"n4ZBWz9C-kEvr-YDfq-9QLi-Q9yPjt8Ly8hL"),sQuery(id+"FL15oFyUtI3aBrd_26.wireOp",EDGE,"e2zvSQfy-2Bil-96lf-zHMV-ZBLVYw9i9ZqR")])]}),"instanceName":"1"});
            var Q17;
            Q17=makeQuery(id+"FVkHQME55aZ6rBw_28.opPattern","COPY",BODY,{"derivedFrom":makeQuery(id+"F8SUDAKNwE7EsUo_26.opExtrude","SWEPT_BODY",BODY,{"disambiguationData":[OSD([sQuery(id+"FL15oFyUtI3aBrd_26.wireOp",EDGE,"r1ENYqX6-6cbb-IXZZ-OYHh-hil2T0saHPIk"),sQuery(id+"FL15oFyUtI3aBrd_26.wireOp",EDGE,"urqhdUsR-mYzn-lPOw-VYYU-hiYjFugUIPjQ"),sQuery(id+"FL15oFyUtI3aBrd_26.wireOp",EDGE,"n4ZBWz9C-kEvr-YDfq-9QLi-Q9yPjt8Ly8hL"),sQuery(id+"FL15oFyUtI3aBrd_26.wireOp",EDGE,"e2zvSQfy-2Bil-96lf-zHMV-ZBLVYw9i9ZqR")])]}),"instanceName":"2"});
            var Q18;
            Q18=makeQuery(id+"FVkHQME55aZ6rBw_28.opPattern","COPY",BODY,{"derivedFrom":makeQuery(id+"F8SUDAKNwE7EsUo_26.opExtrude","SWEPT_BODY",BODY,{"disambiguationData":[OSD([sQuery(id+"FL15oFyUtI3aBrd_26.wireOp",EDGE,"r1ENYqX6-6cbb-IXZZ-OYHh-hil2T0saHPIk"),sQuery(id+"FL15oFyUtI3aBrd_26.wireOp",EDGE,"urqhdUsR-mYzn-lPOw-VYYU-hiYjFugUIPjQ"),sQuery(id+"FL15oFyUtI3aBrd_26.wireOp",EDGE,"n4ZBWz9C-kEvr-YDfq-9QLi-Q9yPjt8Ly8hL"),sQuery(id+"FL15oFyUtI3aBrd_26.wireOp",EDGE,"e2zvSQfy-2Bil-96lf-zHMV-ZBLVYw9i9ZqR")])]}),"instanceName":"3"});
            var Q19;
            Q19=makeQuery(id+"FVkHQME55aZ6rBw_28.opPattern","COPY",BODY,{"derivedFrom":makeQuery(id+"F8SUDAKNwE7EsUo_26.opExtrude","SWEPT_BODY",BODY,{"disambiguationData":[OSD([sQuery(id+"FL15oFyUtI3aBrd_26.wireOp",EDGE,"r1ENYqX6-6cbb-IXZZ-OYHh-hil2T0saHPIk"),sQuery(id+"FL15oFyUtI3aBrd_26.wireOp",EDGE,"urqhdUsR-mYzn-lPOw-VYYU-hiYjFugUIPjQ"),sQuery(id+"FL15oFyUtI3aBrd_26.wireOp",EDGE,"n4ZBWz9C-kEvr-YDfq-9QLi-Q9yPjt8Ly8hL"),sQuery(id+"FL15oFyUtI3aBrd_26.wireOp",EDGE,"e2zvSQfy-2Bil-96lf-zHMV-ZBLVYw9i9ZqR")])]}),"instanceName":"4"});
            var Q20;
            Q20=makeQuery(id+"FVkHQME55aZ6rBw_28.opPattern","COPY",BODY,{"derivedFrom":makeQuery(id+"F8SUDAKNwE7EsUo_26.opExtrude","SWEPT_BODY",BODY,{"disambiguationData":[OSD([sQuery(id+"FL15oFyUtI3aBrd_26.wireOp",EDGE,"r1ENYqX6-6cbb-IXZZ-OYHh-hil2T0saHPIk"),sQuery(id+"FL15oFyUtI3aBrd_26.wireOp",EDGE,"urqhdUsR-mYzn-lPOw-VYYU-hiYjFugUIPjQ"),sQuery(id+"FL15oFyUtI3aBrd_26.wireOp",EDGE,"n4ZBWz9C-kEvr-YDfq-9QLi-Q9yPjt8Ly8hL"),sQuery(id+"FL15oFyUtI3aBrd_26.wireOp",EDGE,"e2zvSQfy-2Bil-96lf-zHMV-ZBLVYw9i9ZqR")])]}),"instanceName":"5"});
            var Q21;
            Q21=makeQuery(id+"FVkHQME55aZ6rBw_28.opPattern","COPY",BODY,{"derivedFrom":makeQuery(id+"F8SUDAKNwE7EsUo_26.opExtrude","SWEPT_BODY",BODY,{"disambiguationData":[OSD([sQuery(id+"FL15oFyUtI3aBrd_26.wireOp",EDGE,"r1ENYqX6-6cbb-IXZZ-OYHh-hil2T0saHPIk"),sQuery(id+"FL15oFyUtI3aBrd_26.wireOp",EDGE,"urqhdUsR-mYzn-lPOw-VYYU-hiYjFugUIPjQ"),sQuery(id+"FL15oFyUtI3aBrd_26.wireOp",EDGE,"n4ZBWz9C-kEvr-YDfq-9QLi-Q9yPjt8Ly8hL"),sQuery(id+"FL15oFyUtI3aBrd_26.wireOp",EDGE,"e2zvSQfy-2Bil-96lf-zHMV-ZBLVYw9i9ZqR")])]}),"instanceName":"6"});
            var Q22;
            Q22=makeQuery(id+"FVkHQME55aZ6rBw_28.opPattern","COPY",BODY,{"derivedFrom":makeQuery(id+"F8SUDAKNwE7EsUo_26.opExtrude","SWEPT_BODY",BODY,{"disambiguationData":[OSD([sQuery(id+"FL15oFyUtI3aBrd_26.wireOp",EDGE,"r1ENYqX6-6cbb-IXZZ-OYHh-hil2T0saHPIk"),sQuery(id+"FL15oFyUtI3aBrd_26.wireOp",EDGE,"urqhdUsR-mYzn-lPOw-VYYU-hiYjFugUIPjQ"),sQuery(id+"FL15oFyUtI3aBrd_26.wireOp",EDGE,"n4ZBWz9C-kEvr-YDfq-9QLi-Q9yPjt8Ly8hL"),sQuery(id+"FL15oFyUtI3aBrd_26.wireOp",EDGE,"e2zvSQfy-2Bil-96lf-zHMV-ZBLVYw9i9ZqR")])]}),"instanceName":"7"});
            var Q23;
            Q23=makeQuery(id+"F8SUDAKNwE7EsUo_26.opExtrude","SWEPT_BODY",BODY,{"disambiguationData":[OSD([sQuery(id+"FL15oFyUtI3aBrd_26.wireOp",EDGE,"VrMjjD4X-CYQ3-yA4v-7hPQ-fvzbZlASwizG"),sQuery(id+"FL15oFyUtI3aBrd_26.wireOp",EDGE,"w2hLujtV-I2TP-pglX-lp1i-IlIAiG8QoFdS"),sQuery(id+"FL15oFyUtI3aBrd_26.wireOp",EDGE,"Haosjz9O-undc-fuWQ-oRTa-weX78iZNw2A3"),sQuery(id+"FL15oFyUtI3aBrd_26.wireOp",EDGE,"bgq73AYN-j48V-VU7J-jVlr-Mn434VgHHMK9")])]});
            var Q24;
            Q24=makeQuery(id+"FeZcZVifgtCtkFP_28.opPattern","COPY",BODY,{"derivedFrom":makeQuery(id+"F8SUDAKNwE7EsUo_26.opExtrude","SWEPT_BODY",BODY,{"disambiguationData":[OSD([sQuery(id+"FL15oFyUtI3aBrd_26.wireOp",EDGE,"r1ENYqX6-6cbb-IXZZ-OYHh-hil2T0saHPIk"),sQuery(id+"FL15oFyUtI3aBrd_26.wireOp",EDGE,"urqhdUsR-mYzn-lPOw-VYYU-hiYjFugUIPjQ"),sQuery(id+"FL15oFyUtI3aBrd_26.wireOp",EDGE,"n4ZBWz9C-kEvr-YDfq-9QLi-Q9yPjt8Ly8hL"),sQuery(id+"FL15oFyUtI3aBrd_26.wireOp",EDGE,"e2zvSQfy-2Bil-96lf-zHMV-ZBLVYw9i9ZqR")])]}),"instanceName":"1"});
            var Q25;
            Q25=makeQuery(id+"FeZcZVifgtCtkFP_28.opPattern","COPY",BODY,{"derivedFrom":makeQuery(id+"F8SUDAKNwE7EsUo_26.opExtrude","SWEPT_BODY",BODY,{"disambiguationData":[OSD([sQuery(id+"FL15oFyUtI3aBrd_26.wireOp",EDGE,"r1ENYqX6-6cbb-IXZZ-OYHh-hil2T0saHPIk"),sQuery(id+"FL15oFyUtI3aBrd_26.wireOp",EDGE,"urqhdUsR-mYzn-lPOw-VYYU-hiYjFugUIPjQ"),sQuery(id+"FL15oFyUtI3aBrd_26.wireOp",EDGE,"n4ZBWz9C-kEvr-YDfq-9QLi-Q9yPjt8Ly8hL"),sQuery(id+"FL15oFyUtI3aBrd_26.wireOp",EDGE,"e2zvSQfy-2Bil-96lf-zHMV-ZBLVYw9i9ZqR")])]}),"instanceName":"2"});
            var Q26;
            Q26=makeQuery(id+"FeZcZVifgtCtkFP_28.opPattern","COPY",BODY,{"derivedFrom":makeQuery(id+"F8SUDAKNwE7EsUo_26.opExtrude","SWEPT_BODY",BODY,{"disambiguationData":[OSD([sQuery(id+"FL15oFyUtI3aBrd_26.wireOp",EDGE,"r1ENYqX6-6cbb-IXZZ-OYHh-hil2T0saHPIk"),sQuery(id+"FL15oFyUtI3aBrd_26.wireOp",EDGE,"urqhdUsR-mYzn-lPOw-VYYU-hiYjFugUIPjQ"),sQuery(id+"FL15oFyUtI3aBrd_26.wireOp",EDGE,"n4ZBWz9C-kEvr-YDfq-9QLi-Q9yPjt8Ly8hL"),sQuery(id+"FL15oFyUtI3aBrd_26.wireOp",EDGE,"e2zvSQfy-2Bil-96lf-zHMV-ZBLVYw9i9ZqR")])]}),"instanceName":"3"});
            var Q27;
            Q27=makeQuery(id+"F8SUDAKNwE7EsUo_26.opExtrude","SWEPT_BODY",BODY,{"disambiguationData":[OSD([sQuery(id+"FL15oFyUtI3aBrd_26.wireOp",EDGE,"r1ENYqX6-6cbb-IXZZ-OYHh-hil2T0saHPIk"),sQuery(id+"FL15oFyUtI3aBrd_26.wireOp",EDGE,"urqhdUsR-mYzn-lPOw-VYYU-hiYjFugUIPjQ"),sQuery(id+"FL15oFyUtI3aBrd_26.wireOp",EDGE,"n4ZBWz9C-kEvr-YDfq-9QLi-Q9yPjt8Ly8hL"),sQuery(id+"FL15oFyUtI3aBrd_26.wireOp",EDGE,"e2zvSQfy-2Bil-96lf-zHMV-ZBLVYw9i9ZqR")])]});
            var Q28;
            Q28=makeQuery(id+"F26.opExtrude","SWEPT_BODY",BODY,{"disambiguationData":[OSD([sQuery(id+"F25.wireOp",EDGE,"E56.0"),sQuery(id+"F25.wireOp",EDGE,"E57.0"),sQuery(id+"F25.wireOp",EDGE,"E58.0"),sQuery(id+"F25.wireOp",EDGE,"E61"),sQuery(id+"F25.wireOp",EDGE,"E62.0"),sQuery(id+"F25.wireOp",EDGE,"E63.0"),sQuery(id+"F25.wireOp",EDGE,"E64.trimOffspring"),sQuery(id+"F25.wireOp",EDGE,"E65.trimOffspring"),sQuery(id+"F25.wireOp",EDGE,"E74"),sQuery(id+"F25.wireOp",EDGE,"E75.MirrorCS")])]});
            var Q29;
            Q29=qCreatedBy(makeId("Right.planeOp"),FACE);
            mirror(context, id + "F27", {"entities" : qUnion([Q0, Q1, Q2, Q3, Q4, Q5, Q6, Q7, Q8, Q9, Q10, Q11, Q12, Q13, Q14, Q15, Q16, Q17, Q18, Q19, Q20, Q21, Q22, Q23, Q24, Q25, Q26, Q27, Q28]), "mirrorPlane" : qUnion([Q29])});
        }
        {
            var Q0;
            Q0=qCreatedBy(makeId("Right.planeOp"),FACE);
            var sketch = newSketch(context, id + "F28", { "sketchPlane" : qUnion([Q0])});
            skLineSegment(sketch, "E77", {"start": v(0, 170.54) * mm, "end": v(370.68, 170.54) * mm});
            skLineSegment(sketch, "E78", {"start": v(370.68, 170.54) * mm, "end": v(370.68, 541.22) * mm});
            skLineSegment(sketch, "E79.0", {"start": v(345.28, 195.94) * mm, "end": v(345.28, 521.37) * mm});
            skLineSegment(sketch, "E80.0", {"start": v(0, 195.94) * mm, "end": v(345.28, 195.94) * mm});
            skLineSegment(sketch, "E81.0", {"start": v(345.28, 521.37) * mm, "end": v(370.68, 541.22) * mm});
            skPoint(sketch, "E82.orphan", {"position": v(2790.83, 2432.05) * mm});
            skPoint(sketch, "E83.orphan", {"position": v(0, 251.61) * mm});
            skLineSegment(sketch, "E84.0", {"start": v(0, 170.54) * mm, "end": v(0, 195.94) * mm});
            skPoint(sketch, "E85.orphan", {"position": v(0, 2133.6) * mm});
            skPoint(sketch, "E86.orphan", {"position": v(0, 0) * mm});
            skSolve(sketch);
        }
        {
            var Q0;
            Q0=qSketchRegion(id+"F28",true);
            extrude(context, id + "F29", {"entities" : qUnion([Q0]), "endBound" : BoundingType.UP_TO_NEXT, "depth" : 25.4 * mm, "offsetDistance" : 25.4 * mm, "hasSecondDirection" : true, "secondDirectionBound" : SecondDirectionBoundingType.UP_TO_NEXT, "secondDirectionOppositeDirection" : true, "secondDirectionDepth" : 25.4 * mm});
        }
        {
            var Q0;
            Q0=sQuery(id+"F25.wireOp",EDGE,"E76");
            cPlane(context, id + "F30", {"entities" : qUnion([Q0]), "cplaneType" : CPlaneType.LINE_ANGLE, "offset" : 25.4 * mm, "angle" : 90 * degree, "width" : 152.4 * mm, "height" : 152.4 * mm});
        }
        {
            var Q0;
            Q0=qCreatedBy(id+"F30.planeOp",FACE);
            var sketch = newSketch(context, id + "F31", { "sketchPlane" : qUnion([Q0])});
            skLineSegment(sketch, "E87", {"start": v(-500.06, 751.75) * mm, "end": v(-500.06, 675.1) * mm, "construction": true});
            skLineSegment(sketch, "E88", {"start": v(-500.06, 675.1) * mm, "end": v(-500.06, 598.43) * mm, "construction": true});
            skLineSegment(sketch, "E89", {"start": v(-500.06, 598.43) * mm, "end": v(-500.06, 521.77) * mm, "construction": true});
            skLineSegment(sketch, "E90", {"start": v(-500.06, 521.77) * mm, "end": v(-500.06, 445.11) * mm, "construction": true});
            skLineSegment(sketch, "E91", {"start": v(-500.06, 445.11) * mm, "end": v(-500.06, 368.45) * mm, "construction": true});
            skCircle(sketch, "E92", {"center": v(-500.06, 675.1) * mm, "radius": 1.59 * mm});
            skCircle(sketch, "E93", {"center": v(-500.06, 598.43) * mm, "radius": 1.59 * mm});
            skCircle(sketch, "E94", {"center": v(-500.06, 521.77) * mm, "radius": 1.59 * mm});
            skCircle(sketch, "E95", {"center": v(-500.06, 445.11) * mm, "radius": 1.59 * mm});
            skSolve(sketch);
        }
        {
            var Q0;
            Q0 = qSketchRegion(id + "F31", true);
            var Q1;
            Q1=makeQuery(id+"F26.opExtrude","SWEPT_FACE",FACE,{"disambiguationData":[OSD([sQuery(id+"F25.wireOp",EDGE,"E64.trimOffspring")])]});
            var Q2;
            Q2=makeQuery(id+"F26.opExtrude","SWEPT_FACE",FACE,{"disambiguationData":[OSD([sQuery(id+"F25.wireOp",EDGE,"E63.0")])]});
            extrude(context, id + "F32", {"entities" : qUnion([Q0]), "operationType" : NewBodyOperationType.ADD, "endBound" : BoundingType.UP_TO_SURFACE, "depth" : 25.4 * mm, "endBoundEntityFace" : qUnion([Q1]), "offsetDistance" : 25.4 * mm, "hasSecondDirection" : true, "secondDirectionBound" : SecondDirectionBoundingType.UP_TO_SURFACE, "secondDirectionOppositeDirection" : true, "secondDirectionDepth" : 25.4 * mm, "secondDirectionBoundEntityFace" : qUnion([Q2])});
        }
        {
            var Q0;
            Q0=makeQuery(id+"F16.opExtrude","SWEPT_FACE",FACE,{"disambiguationData":[OSD([sQuery(id+"F15.wireOp",EDGE,"E27.top")])]});
            var sketch = newSketch(context, id + "F33", { "sketchPlane" : qUnion([Q0])});
            skLineSegment(sketch, "E96.bottom", {"start": v(615.95, -152.4) * mm, "end": v(577.85, -152.4) * mm});
            skLineSegment(sketch, "E96.top", {"start": v(615.95, -203.2) * mm, "end": v(577.85, -203.2) * mm});
            skLineSegment(sketch, "E96.left", {"start": v(615.95, -152.4) * mm, "end": v(615.95, -203.2) * mm});
            skLineSegment(sketch, "E96.right", {"start": v(577.85, -152.4) * mm, "end": v(577.85, -203.2) * mm});
            skLineSegment(sketch, "E97.bottom", {"start": v(615.95, -1397) * mm, "end": v(577.85, -1397) * mm});
            skLineSegment(sketch, "E97.top", {"start": v(615.95, -1346.2) * mm, "end": v(577.85, -1346.2) * mm});
            skLineSegment(sketch, "E97.left", {"start": v(615.95, -1397) * mm, "end": v(615.95, -1346.2) * mm});
            skLineSegment(sketch, "E97.right", {"start": v(577.85, -1397) * mm, "end": v(577.85, -1346.2) * mm});
            skLineSegment(sketch, "E98.0.0", {"start": v(577.85, -1552.58) * mm, "end": v(577.85, -1614) * mm});
            skLineSegment(sketch, "E98.0.1", {"start": v(577.85, -2860.68) * mm, "end": v(615.95, -2860.68) * mm});
            skLineSegment(sketch, "E98.0.2", {"start": v(615.95, -1614) * mm, "end": v(615.95, -1552.58) * mm});
            skLineSegment(sketch, "E98.0.3", {"start": v(615.95, -1552.58) * mm, "end": v(577.85, -1552.58) * mm});
            skLineSegment(sketch, "E99.0.2", {"start": v(615.95, -1614) * mm, "end": v(615.95, -1563.2) * mm});
            skLineSegment(sketch, "E100", {"start": v(615.95, -1614) * mm, "end": v(577.85, -1614) * mm});
            skLineSegment(sketch, "E101", {"start": v(615.95, -1563.2) * mm, "end": v(577.85, -1563.2) * mm});
            skLineSegment(sketch, "E102.trimOffspring", {"start": v(577.85, -1563.2) * mm, "end": v(577.85, -1614) * mm});
            skSolve(sketch);
        }
        {
            var Q0;
            Q0 = qSketchRegion(id + "F33", true);
            extrude(context, id + "F34", {"entities" : qUnion([Q0]), "endBound" : BoundingType.UP_TO_NEXT, "depth" : 25.4 * mm, "offsetDistance" : 25.4 * mm});
        }
    });
